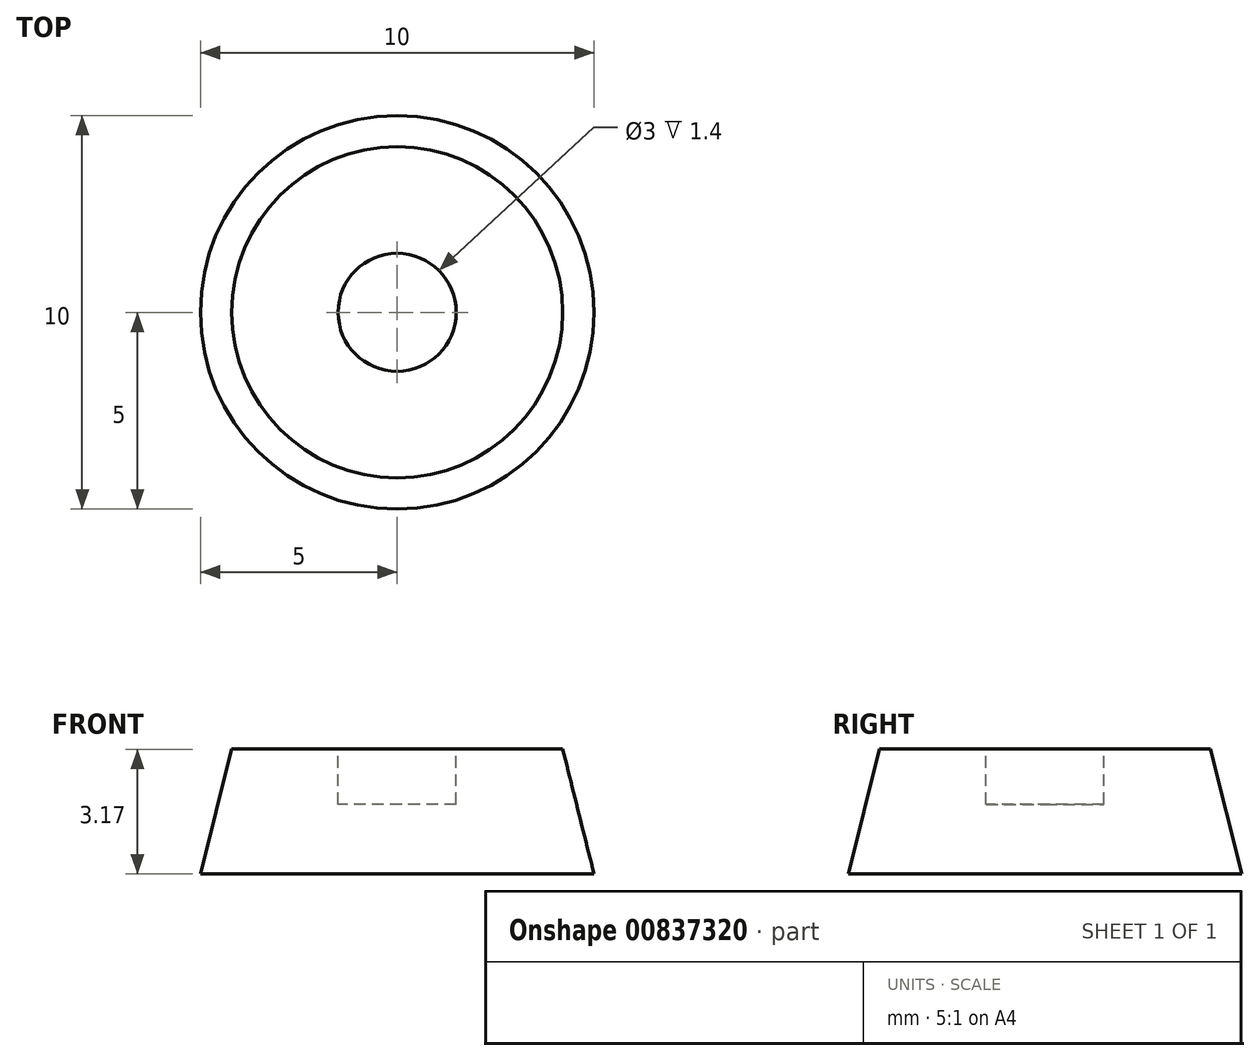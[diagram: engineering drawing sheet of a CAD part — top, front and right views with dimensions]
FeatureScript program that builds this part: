
annotation { "Feature Type Name" : "Feature", "Feature Type Description" : "" }
export const myFeature = defineFeature(function(context is Context, id is Id, definition is map)
    precondition{}
    {
        {
            var Q0;
            Q0=qCreatedBy(makeId("Top.planeOp"),FACE);
            var sketch = newSketch(context, id + "F0", { "sketchPlane" : qUnion([Q0])});
            skCircle(sketch, "E0", {"center": v(0, 0) * mm, "radius": 5 * mm});
            skSolve(sketch);
        }
        {
            var Q0;
            Q0=qCreatedBy(makeId("Right.planeOp"),FACE);
            var sketch = newSketch(context, id + "F1", { "sketchPlane" : qUnion([Q0])});
            skPoint(sketch, "E1", {"position": v(0, 19.96) * mm});
            skSolve(sketch);
        }
        {
            var Q0;
            Q0=makeQuery(id+"F0.imprint","IMPRINT",FACE,{"disambiguationData":[TD([[makeQuery(id+"F0.imprint","IMPRINT",EDGE,{"derivedFrom":sQuery(id+"F0.wireOp",EDGE,"E0")}),1.0]])]});
            var Q1;
            Q1=sQuery(id+"F1.wireOp",VERTEX,"E1");
            loft(context, id + "F2", {"sheetProfilesArray" : [{ "sheetProfileEntities" : qUnion([Q0]) }, { "sheetProfileEntities" : qUnion([Q1]) }]});
        }
        {
            var Q0;
            Q0=qCreatedBy(makeId("Right.planeOp"),FACE);
            var sketch = newSketch(context, id + "F3", { "sketchPlane" : qUnion([Q0])});
            skLineSegment(sketch, "E2.bottom", {"start": v(13.12, 23.17) * mm, "end": v(-13.12, 23.17) * mm});
            skLineSegment(sketch, "E2.top", {"start": v(13.12, 3.17) * mm, "end": v(-13.12, 3.17) * mm});
            skLineSegment(sketch, "E2.left", {"start": v(13.12, 23.17) * mm, "end": v(13.12, 3.17) * mm});
            skLineSegment(sketch, "E2.right", {"start": v(-13.12, 23.17) * mm, "end": v(-13.12, 3.17) * mm});
            skPoint(sketch, "E2.middle", {"position": v(0, 13.17) * mm});
            skSolve(sketch);
        }
        {
            var Q0;
            Q0=makeQuery(id+"F3.imprint","IMPRINT",FACE,{"disambiguationData":[TD([[makeQuery(id+"F3.imprint","IMPRINT",EDGE,{"derivedFrom":sQuery(id+"F3.wireOp",EDGE,"E2.bottom")}),1.0]])]});
            extrude(context, id + "F4", {"entities" : qUnion([Q0]), "operationType" : NewBodyOperationType.REMOVE, "endBound" : BoundingType.SYMMETRIC, "oppositeDirection" : true, "depth" : 25 * mm, "offsetDistance" : 25 * mm});
        }
        {
            var Q0;
            Q0=makeQuery(id+"F4.boolean.opBoolean","COPY",FACE,{"derivedFrom":makeQuery(id+"F4.opExtrude","SWEPT_FACE",FACE,{"disambiguationData":[OSD([sQuery(id+"F3.wireOp",EDGE,"E2.top")])]})});
            var sketch = newSketch(context, id + "F5", { "sketchPlane" : qUnion([Q0])});
            skCircle(sketch, "E3", {"center": v(0, 0) * mm, "radius": 1.5 * mm});
            skSolve(sketch);
        }
        {
            var Q0;
            Q0=makeQuery(id+"F5.imprint","IMPRINT",FACE,{"disambiguationData":[TD([[makeQuery(id+"F5.imprint","IMPRINT",EDGE,{"derivedFrom":sQuery(id+"F5.wireOp",EDGE,"E3")}),1.0]])]});
            extrude(context, id + "F6", {"entities" : qUnion([Q0]), "operationType" : NewBodyOperationType.REMOVE, "oppositeDirection" : true, "depth" : 1.4 * mm, "offsetDistance" : 25 * mm});
        }
    });
